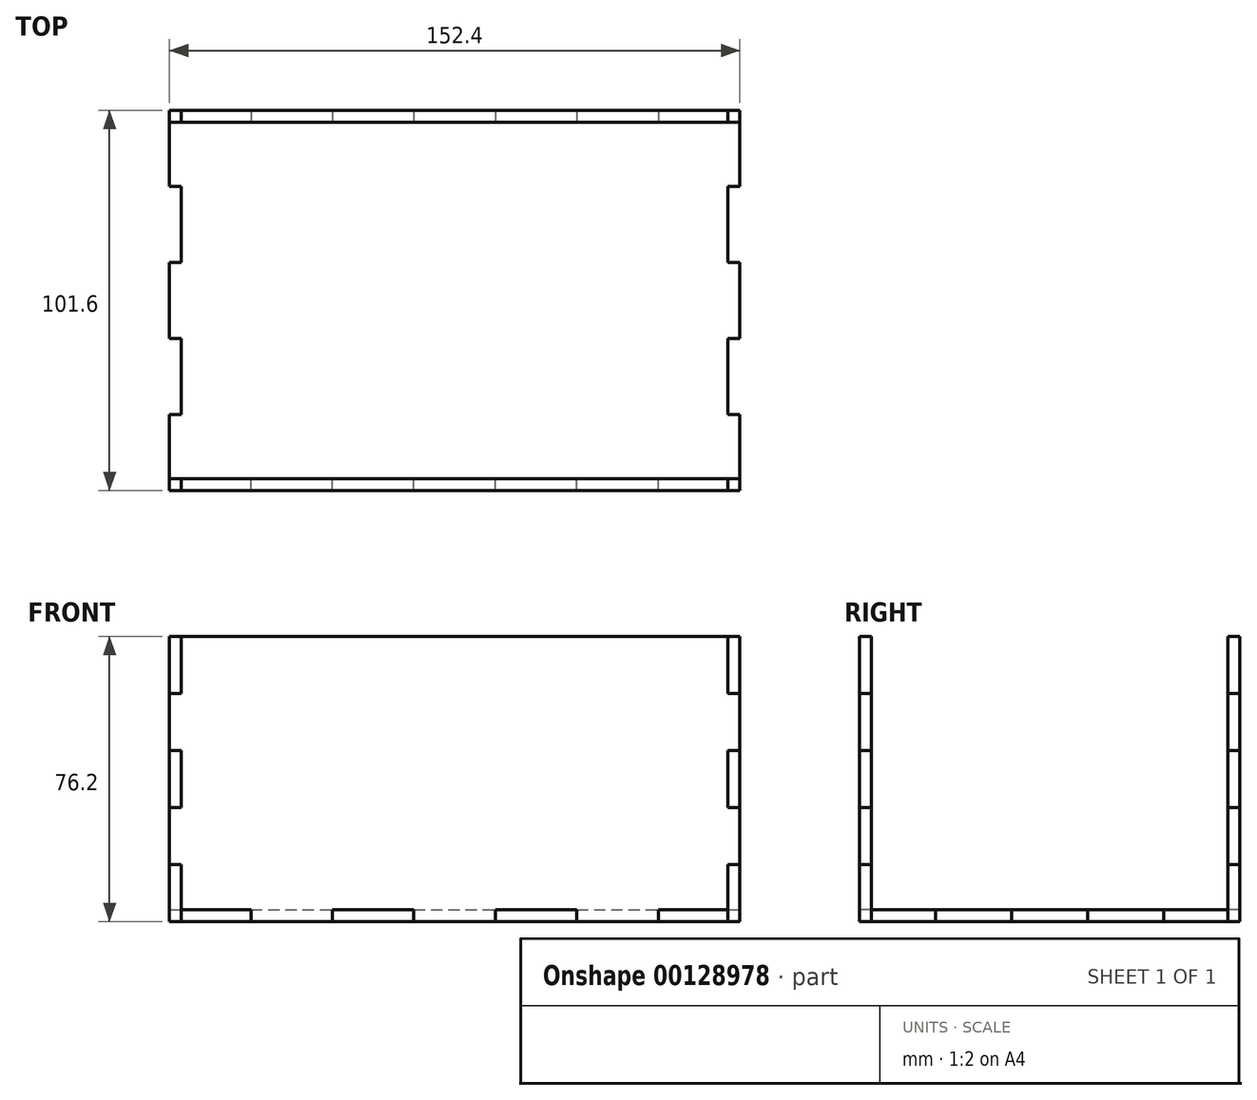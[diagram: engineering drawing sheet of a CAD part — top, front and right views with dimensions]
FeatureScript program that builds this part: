
annotation { "Feature Type Name" : "Feature", "Feature Type Description" : "" }
export const myFeature = defineFeature(function(context is Context, id is Id, definition is map)
    precondition{}
    {
        {
            var Q0;
            Q0=qCreatedBy(makeId("Top.planeOp"),FACE);
            var sketch = newSketch(context, id + "F0", { "sketchPlane" : qUnion([Q0])});
            skLineSegment(sketch, "E0.bottom", {"start": v(76.2, 50.8) * mm, "end": v(-76.2, 50.8) * mm});
            skLineSegment(sketch, "E0.top", {"start": v(76.2, -50.8) * mm, "end": v(-76.2, -50.8) * mm});
            skLineSegment(sketch, "E0.left", {"start": v(76.2, 50.8) * mm, "end": v(76.2, -50.8) * mm});
            skLineSegment(sketch, "E0.right", {"start": v(-76.2, 50.8) * mm, "end": v(-76.2, -50.8) * mm});
            skPoint(sketch, "E0.middle", {"position": v(0, 0) * mm});
            skLineSegment(sketch, "E1", {"start": v(-76.2, 50.8) * mm, "end": v(-73.03, 50.8) * mm});
            skLineSegment(sketch, "E2.0.1.0", {"start": v(-76.2, 30.48) * mm, "end": v(-73.03, 30.48) * mm});
            skLineSegment(sketch, "E2.0.2.0", {"start": v(-76.2, 10.16) * mm, "end": v(-73.03, 10.16) * mm});
            skLineSegment(sketch, "E2.0.3.0", {"start": v(-76.2, -10.16) * mm, "end": v(-73.02, -10.16) * mm});
            skLineSegment(sketch, "E2.0.4.0", {"start": v(-76.2, -30.48) * mm, "end": v(-73.02, -30.48) * mm});
            skLineSegment(sketch, "E2.0.5.0", {"start": v(-76.2, -50.8) * mm, "end": v(-73.02, -50.8) * mm});
            skLineSegment(sketch, "E2.direction1", {"start": v(-76.2, 50.8) * mm, "end": v(-50.8, 50.8) * mm, "construction": true});
            skLineSegment(sketch, "E2.direction2", {"start": v(-76.2, 50.8) * mm, "end": v(-76.2, 30.48) * mm, "construction": true});
            skLineSegment(sketch, "E3", {"start": v(-73.03, 50.8) * mm, "end": v(-73.03, -50.8) * mm});
            skLineSegment(sketch, "E4.MirrorCS", {"start": v(73.03, 50.8) * mm, "end": v(73.03, -50.8) * mm});
            skLineSegment(sketch, "E5.MirrorCS", {"start": v(76.2, 50.8) * mm, "end": v(76.2, 30.48) * mm, "construction": true});
            skLineSegment(sketch, "E6.MirrorCS", {"start": v(76.2, -50.8) * mm, "end": v(73.02, -50.8) * mm});
            skLineSegment(sketch, "E7.MirrorCS", {"start": v(76.2, -30.48) * mm, "end": v(73.02, -30.48) * mm});
            skLineSegment(sketch, "E8.MirrorCS", {"start": v(76.2, -10.16) * mm, "end": v(73.02, -10.16) * mm});
            skLineSegment(sketch, "E9.MirrorCS", {"start": v(76.2, 10.16) * mm, "end": v(73.03, 10.16) * mm});
            skLineSegment(sketch, "E10.MirrorCS", {"start": v(76.2, 30.48) * mm, "end": v(73.03, 30.48) * mm});
            skLineSegment(sketch, "E11.MirrorCS", {"start": v(76.2, 50.8) * mm, "end": v(73.03, 50.8) * mm});
            skLineSegment(sketch, "E12", {"start": v(-76.2, 50.8) * mm, "end": v(-76.2, 47.63) * mm});
            skLineSegment(sketch, "E13.1.0.0", {"start": v(-54.43, 50.8) * mm, "end": v(-54.43, 47.63) * mm});
            skLineSegment(sketch, "E13.2.0.0", {"start": v(-32.66, 50.8) * mm, "end": v(-32.66, 47.63) * mm});
            skLineSegment(sketch, "E13.3.0.0", {"start": v(-10.89, 50.8) * mm, "end": v(-10.89, 47.63) * mm});
            skLineSegment(sketch, "E13.4.0.0", {"start": v(10.89, 50.8) * mm, "end": v(10.89, 47.63) * mm});
            skLineSegment(sketch, "E13.5.0.0", {"start": v(32.66, 50.8) * mm, "end": v(32.66, 47.63) * mm});
            skLineSegment(sketch, "E13.6.0.0", {"start": v(54.43, 50.8) * mm, "end": v(54.43, 47.63) * mm});
            skLineSegment(sketch, "E13.7.0.0", {"start": v(76.2, 50.8) * mm, "end": v(76.2, 47.63) * mm});
            skLineSegment(sketch, "E13.direction1", {"start": v(-76.2, 47.62) * mm, "end": v(-54.43, 47.62) * mm, "construction": true});
            skLineSegment(sketch, "E14", {"start": v(-76.2, 47.62) * mm, "end": v(76.2, 47.63) * mm});
            skLineSegment(sketch, "E15.MirrorCS", {"start": v(-76.2, -50.8) * mm, "end": v(-76.2, -47.63) * mm});
            skLineSegment(sketch, "E16.MirrorCS", {"start": v(76.2, -50.8) * mm, "end": v(73.03, -50.8) * mm});
            skLineSegment(sketch, "E17.MirrorCS", {"start": v(-76.2, -50.8) * mm, "end": v(-73.03, -50.8) * mm});
            skLineSegment(sketch, "E18.MirrorCS", {"start": v(76.2, -50.8) * mm, "end": v(76.2, -47.63) * mm});
            skLineSegment(sketch, "E19.MirrorCS", {"start": v(-10.89, -50.8) * mm, "end": v(-10.89, -47.63) * mm});
            skLineSegment(sketch, "E20.MirrorCS", {"start": v(10.89, -50.8) * mm, "end": v(10.89, -47.63) * mm});
            skLineSegment(sketch, "E21.MirrorCS", {"start": v(54.43, -50.8) * mm, "end": v(54.43, -47.63) * mm});
            skLineSegment(sketch, "E22.MirrorCS", {"start": v(-32.66, -50.8) * mm, "end": v(-32.66, -47.63) * mm});
            skLineSegment(sketch, "E23.MirrorCS", {"start": v(-54.43, -50.8) * mm, "end": v(-54.43, -47.63) * mm});
            skLineSegment(sketch, "E24.MirrorCS", {"start": v(32.66, -50.8) * mm, "end": v(32.66, -47.63) * mm});
            skLineSegment(sketch, "E25.MirrorCS", {"start": v(-76.2, -47.62) * mm, "end": v(76.2, -47.63) * mm});
            skLineSegment(sketch, "E26.MirrorCS", {"start": v(-76.2, -47.62) * mm, "end": v(-54.43, -47.62) * mm, "construction": true});
            skLineSegment(sketch, "E27.MirrorCS", {"start": v(-76.2, -50.8) * mm, "end": v(-50.8, -50.8) * mm, "construction": true});
            skSolve(sketch);
        }
        {
            var Q0;
            {var subQ0=sQuery(id+"F0.wireOp",EDGE,"E1");Q0=makeQuery(id+"F0.imprint","IMPRINT",FACE,{"disambiguationData":[TD([[makeQuery(id+"F0.imprint","IMPRINT",EDGE,{"derivedFrom":subQ0}),-1.0]])]});}
            var Q1;
            {var subQ3=sQuery(id+"F0.wireOp",EDGE,"E13.1.0.0");Q1=makeQuery(id+"F0.imprint","IMPRINT",FACE,{"disambiguationData":[TD([[makeQuery(id+"F0.imprint","IMPRINT",EDGE,{"derivedFrom":subQ3}),-1.0]])]});}
            var Q2;
            {var subQ3=sQuery(id+"F0.wireOp",EDGE,"E2.0.1.0");Q2=makeQuery(id+"F0.imprint","IMPRINT",FACE,{"disambiguationData":[TD([[makeQuery(id+"F0.imprint","IMPRINT",EDGE,{"derivedFrom":subQ3}),1.0]])]});}
            var Q3;
            {var subQ4=sQuery(id+"F0.wireOp",EDGE,"E3");var subQ23=makeQuery(id+"F0.imprint","INTERSECT",VERTEX,{"derivedFrom":[sQuery(id+"F0.wireOp",EDGE,"E2.0.1.0"),subQ4]});Q3=makeQuery(id+"F0.imprint","IMPRINT",FACE,{"disambiguationData":[TD([[makeQuery(id+"F0.imprint","IMPRINT",EDGE,{"disambiguationData":[TD([[subQ23,1.0]])],"derivedFrom":subQ4}),1.0]])]});}
            var Q4;
            {var subQ0=sQuery(id+"F0.wireOp",EDGE,"E2.0.2.0");Q4=makeQuery(id+"F0.imprint","IMPRINT",FACE,{"disambiguationData":[TD([[makeQuery(id+"F0.imprint","IMPRINT",EDGE,{"derivedFrom":subQ0}),-1.0]])]});}
            var Q5;
            {var subQ3=sQuery(id+"F0.wireOp",EDGE,"E2.0.4.0");Q5=makeQuery(id+"F0.imprint","IMPRINT",FACE,{"disambiguationData":[TD([[makeQuery(id+"F0.imprint","IMPRINT",EDGE,{"derivedFrom":subQ3}),-1.0]])]});}
            var Q6;
            {var subQ5=sQuery(id+"F0.wireOp",EDGE,"E15.MirrorCS");Q6=makeQuery(id+"F0.imprint","IMPRINT",FACE,{"disambiguationData":[TD([[makeQuery(id+"F0.imprint","IMPRINT",EDGE,{"derivedFrom":subQ5}),-1.0]])]});}
            var Q7;
            {var subQ5=sQuery(id+"F0.wireOp",EDGE,"E23.MirrorCS");Q7=makeQuery(id+"F0.imprint","IMPRINT",FACE,{"disambiguationData":[TD([[makeQuery(id+"F0.imprint","IMPRINT",EDGE,{"derivedFrom":subQ5}),1.0]])]});}
            var Q8;
            {var subQ0=sQuery(id+"F0.wireOp",EDGE,"E19.MirrorCS");Q8=makeQuery(id+"F0.imprint","IMPRINT",FACE,{"disambiguationData":[TD([[makeQuery(id+"F0.imprint","IMPRINT",EDGE,{"derivedFrom":subQ0}),1.0]])]});}
            var Q9;
            {var subQ0=sQuery(id+"F0.wireOp",EDGE,"E20.MirrorCS");Q9=makeQuery(id+"F0.imprint","IMPRINT",FACE,{"disambiguationData":[TD([[makeQuery(id+"F0.imprint","IMPRINT",EDGE,{"derivedFrom":subQ0}),-1.0]])]});}
            var Q10;
            {var subQ5=sQuery(id+"F0.wireOp",EDGE,"E21.MirrorCS");Q10=makeQuery(id+"F0.imprint","IMPRINT",FACE,{"disambiguationData":[TD([[makeQuery(id+"F0.imprint","IMPRINT",EDGE,{"derivedFrom":subQ5}),-1.0]])]});}
            var Q11;
            {var subQ5=sQuery(id+"F0.wireOp",EDGE,"E18.MirrorCS");Q11=makeQuery(id+"F0.imprint","IMPRINT",FACE,{"disambiguationData":[TD([[makeQuery(id+"F0.imprint","IMPRINT",EDGE,{"derivedFrom":subQ5}),1.0]])]});}
            var Q12;
            {var subQ0=sQuery(id+"F0.wireOp",EDGE,"E7.MirrorCS");Q12=makeQuery(id+"F0.imprint","IMPRINT",FACE,{"disambiguationData":[TD([[makeQuery(id+"F0.imprint","IMPRINT",EDGE,{"derivedFrom":subQ0}),1.0]])]});}
            var Q13;
            {var subQ0=sQuery(id+"F0.wireOp",EDGE,"E8.MirrorCS");Q13=makeQuery(id+"F0.imprint","IMPRINT",FACE,{"disambiguationData":[TD([[makeQuery(id+"F0.imprint","IMPRINT",EDGE,{"derivedFrom":subQ0}),-1.0]])]});}
            var Q14;
            {var subQ0=sQuery(id+"F0.wireOp",EDGE,"E10.MirrorCS");Q14=makeQuery(id+"F0.imprint","IMPRINT",FACE,{"disambiguationData":[TD([[makeQuery(id+"F0.imprint","IMPRINT",EDGE,{"derivedFrom":subQ0}),-1.0]])]});}
            var Q15;
            {var subQ0=sQuery(id+"F0.wireOp",EDGE,"E11.MirrorCS");Q15=makeQuery(id+"F0.imprint","IMPRINT",FACE,{"disambiguationData":[TD([[makeQuery(id+"F0.imprint","IMPRINT",EDGE,{"derivedFrom":subQ0}),1.0]])]});}
            var Q16;
            {var subQ3=sQuery(id+"F0.wireOp",EDGE,"E13.6.0.0");Q16=makeQuery(id+"F0.imprint","IMPRINT",FACE,{"disambiguationData":[TD([[makeQuery(id+"F0.imprint","IMPRINT",EDGE,{"derivedFrom":subQ3}),1.0]])]});}
            var Q17;
            {var subQ0=sQuery(id+"F0.wireOp",EDGE,"E13.4.0.0");Q17=makeQuery(id+"F0.imprint","IMPRINT",FACE,{"disambiguationData":[TD([[makeQuery(id+"F0.imprint","IMPRINT",EDGE,{"derivedFrom":subQ0}),1.0]])]});}
            var Q18;
            {var subQ0=sQuery(id+"F0.wireOp",EDGE,"E13.2.0.0");Q18=makeQuery(id+"F0.imprint","IMPRINT",FACE,{"disambiguationData":[TD([[makeQuery(id+"F0.imprint","IMPRINT",EDGE,{"derivedFrom":subQ0}),1.0]])]});}
            extrude(context, id + "F1", {"entities" : qUnion([Q0, Q1, Q2, Q3, Q4, Q5, Q6, Q7, Q8, Q9, Q10, Q11, Q12, Q13, Q14, Q15, Q16, Q17, Q18]), "depth" : 3.17 * mm});
        }
        {
            var Q0;
            Q0=makeQuery(id+"F1.opExtrude","SWEPT_FACE",FACE,{"disambiguationData":[OSD([sQuery(id+"F0.wireOp",EDGE,"E0.left"),sQuery(id+"F0.wireOp",EDGE,"E18.MirrorCS")])]});
            var sketch = newSketch(context, id + "F2", { "sketchPlane" : qUnion([Q0])});
            skLineSegment(sketch, "E28.bottom", {"start": v(-50.8, 0) * mm, "end": v(50.8, 0) * mm});
            skLineSegment(sketch, "E28.top", {"start": v(-50.8, 76.2) * mm, "end": v(50.8, 76.2) * mm});
            skLineSegment(sketch, "E28.left", {"start": v(-50.8, 0) * mm, "end": v(-50.8, 76.2) * mm});
            skLineSegment(sketch, "E28.right", {"start": v(50.8, 0) * mm, "end": v(50.8, 76.2) * mm});
            skLineSegment(sketch, "E29", {"start": v(-50.8, 76.2) * mm, "end": v(-47.62, 76.2) * mm});
            skLineSegment(sketch, "E30.0.1.0", {"start": v(-50.8, 60.96) * mm, "end": v(-47.62, 60.96) * mm});
            skLineSegment(sketch, "E30.0.2.0", {"start": v(-50.8, 45.72) * mm, "end": v(-47.62, 45.72) * mm});
            skLineSegment(sketch, "E30.0.3.0", {"start": v(-50.8, 30.48) * mm, "end": v(-47.62, 30.48) * mm});
            skLineSegment(sketch, "E30.0.4.0", {"start": v(-50.8, 15.24) * mm, "end": v(-47.62, 15.24) * mm});
            skLineSegment(sketch, "E30.0.5.0", {"start": v(-50.8, 0) * mm, "end": v(-47.62, 0) * mm});
            skLineSegment(sketch, "E30.direction1", {"start": v(-50.8, 76.2) * mm, "end": v(-25.4, 76.2) * mm, "construction": true});
            skLineSegment(sketch, "E30.direction2", {"start": v(-50.8, 76.2) * mm, "end": v(-50.8, 60.96) * mm, "construction": true});
            skLineSegment(sketch, "E31", {"start": v(-47.62, 76.2) * mm, "end": v(-47.62, 0) * mm});
            skLineSegment(sketch, "E32.MirrorCS", {"start": v(50.8, 76.2) * mm, "end": v(47.63, 76.2) * mm});
            skLineSegment(sketch, "E33.MirrorCS", {"start": v(50.8, 30.48) * mm, "end": v(47.63, 30.48) * mm});
            skLineSegment(sketch, "E34.MirrorCS", {"start": v(50.8, 60.96) * mm, "end": v(47.63, 60.96) * mm});
            skLineSegment(sketch, "E35.MirrorCS", {"start": v(50.8, 45.72) * mm, "end": v(47.63, 45.72) * mm});
            skLineSegment(sketch, "E36.MirrorCS", {"start": v(50.8, 15.24) * mm, "end": v(47.63, 15.24) * mm});
            skLineSegment(sketch, "E37.MirrorCS", {"start": v(50.8, 0) * mm, "end": v(47.63, 0) * mm});
            skLineSegment(sketch, "E38.MirrorCS", {"start": v(50.8, 76.2) * mm, "end": v(50.8, 60.96) * mm, "construction": true});
            skLineSegment(sketch, "E39.MirrorCS", {"start": v(47.63, 76.2) * mm, "end": v(47.63, 0) * mm});
            skSolve(sketch);
        }
        {
            var Q0;
            {var subQ0=sQuery(id+"F2.wireOp",EDGE,"E29");Q0=makeQuery(id+"F2.imprint","IMPRINT",FACE,{"disambiguationData":[TD([[makeQuery(id+"F2.imprint","IMPRINT",EDGE,{"derivedFrom":subQ0}),-1.0]])]});}
            var Q1;
            {var subQ3=sQuery(id+"F2.wireOp",EDGE,"E28.top");Q1=makeQuery(id+"F2.imprint","IMPRINT",FACE,{"disambiguationData":[TD([[makeQuery(id+"F2.imprint","IMPRINT",EDGE,{"derivedFrom":subQ3}),-1.0]])]});}
            var Q2;
            {var subQ0=sQuery(id+"F2.wireOp",EDGE,"E30.0.2.0");Q2=makeQuery(id+"F2.imprint","IMPRINT",FACE,{"disambiguationData":[TD([[makeQuery(id+"F2.imprint","IMPRINT",EDGE,{"derivedFrom":subQ0}),-1.0]])]});}
            var Q3;
            {var subQ3=sQuery(id+"F2.wireOp",EDGE,"E30.0.4.0");Q3=makeQuery(id+"F2.imprint","IMPRINT",FACE,{"disambiguationData":[TD([[makeQuery(id+"F2.imprint","IMPRINT",EDGE,{"derivedFrom":subQ3}),-1.0]])]});}
            var Q4;
            {var subQ0=sQuery(id+"F2.wireOp",EDGE,"E30.0.5.0");Q4=makeQuery(id+"F2.imprint","IMPRINT",FACE,{"disambiguationData":[TD([[makeQuery(id+"F2.imprint","IMPRINT",EDGE,{"derivedFrom":subQ0}),1.0]])]});}
            var Q5;
            {var subQ1=sQuery(id+"F0.wireOp",EDGE,"E0.left");var subQ2=makeQuery(id+"F1.opExtrude","SWEPT_EDGE",EDGE,{"disambiguationData":[OSD([sQuery(id+"F0.wireOp",EDGE,"E7.MirrorCS"),subQ1])]});Q5=makeQuery(id+"F2.imprint","IMPRINT",FACE,{"disambiguationData":[TD([[makeQuery(id+"F2.imprint","IMPRINT",EDGE,{"derivedFrom":subQ2}),-1.0]])]});}
            var Q6;
            {var subQ2=sQuery(id+"F2.wireOp",EDGE,"E36.MirrorCS");Q6=makeQuery(id+"F2.imprint","IMPRINT",FACE,{"disambiguationData":[TD([[makeQuery(id+"F2.imprint","IMPRINT",EDGE,{"derivedFrom":subQ2}),1.0]])]});}
            var Q7;
            {var subQ0=sQuery(id+"F2.wireOp",EDGE,"E33.MirrorCS");Q7=makeQuery(id+"F2.imprint","IMPRINT",FACE,{"disambiguationData":[TD([[makeQuery(id+"F2.imprint","IMPRINT",EDGE,{"derivedFrom":subQ0}),-1.0]])]});}
            var Q8;
            {var subQ0=sQuery(id+"F2.wireOp",EDGE,"E32.MirrorCS");Q8=makeQuery(id+"F2.imprint","IMPRINT",FACE,{"disambiguationData":[TD([[makeQuery(id+"F2.imprint","IMPRINT",EDGE,{"derivedFrom":subQ0}),1.0]])]});}
            extrude(context, id + "F3", {"entities" : qUnion([Q0, Q1, Q2, Q3, Q4, Q5, Q6, Q7, Q8]), "oppositeDirection" : true, "depth" : 3.17 * mm});
        }
        {
            var Q0;
            Q0=makeQuery(id+"F3.opExtrude","SWEPT_BODY",BODY,{"disambiguationData":[OSD([sQuery(id+"F2.wireOp",EDGE,"E28.bottom"),sQuery(id+"F2.wireOp",EDGE,"E28.top"),sQuery(id+"F2.wireOp",EDGE,"E28.left"),sQuery(id+"F2.wireOp",EDGE,"E29"),sQuery(id+"F2.wireOp",EDGE,"E30.0.1.0"),sQuery(id+"F2.wireOp",EDGE,"E30.0.2.0"),sQuery(id+"F2.wireOp",EDGE,"E30.0.3.0"),sQuery(id+"F2.wireOp",EDGE,"E30.0.4.0"),sQuery(id+"F2.wireOp",EDGE,"E30.0.5.0"),sQuery(id+"F2.wireOp",EDGE,"E31"),sQuery(id+"F2.wireOp",EDGE,"E28.right"),sQuery(id+"F2.wireOp",EDGE,"E32.MirrorCS"),sQuery(id+"F2.wireOp",EDGE,"E33.MirrorCS"),sQuery(id+"F2.wireOp",EDGE,"E34.MirrorCS"),sQuery(id+"F2.wireOp",EDGE,"E35.MirrorCS"),sQuery(id+"F2.wireOp",EDGE,"E36.MirrorCS"),sQuery(id+"F2.wireOp",EDGE,"E37.MirrorCS"),sQuery(id+"F2.wireOp",EDGE,"E39.MirrorCS")])]});
            var Q1;
            Q1=qCreatedBy(makeId("Right.planeOp"),FACE);
            mirror(context, id + "F4", {"entities" : qUnion([Q0]), "mirrorPlane" : qUnion([Q1])});
        }
        {
            var Q0;
            Q0=makeQuery(id+"F1.opExtrude","SWEPT_BODY",BODY,{"disambiguationData":[OSD([sQuery(id+"F0.wireOp",EDGE,"E0.bottom"),sQuery(id+"F0.wireOp",EDGE,"E0.right"),sQuery(id+"F0.wireOp",EDGE,"E1"),sQuery(id+"F0.wireOp",EDGE,"E2.0.1.0"),sQuery(id+"F0.wireOp",EDGE,"E2.0.2.0"),sQuery(id+"F0.wireOp",EDGE,"E2.0.3.0"),sQuery(id+"F0.wireOp",EDGE,"E2.0.4.0"),sQuery(id+"F0.wireOp",EDGE,"E3"),sQuery(id+"F0.wireOp",EDGE,"E4.MirrorCS"),sQuery(id+"F0.wireOp",EDGE,"E7.MirrorCS"),sQuery(id+"F0.wireOp",EDGE,"E0.left"),sQuery(id+"F0.wireOp",EDGE,"E8.MirrorCS"),sQuery(id+"F0.wireOp",EDGE,"E9.MirrorCS"),sQuery(id+"F0.wireOp",EDGE,"E10.MirrorCS"),sQuery(id+"F0.wireOp",EDGE,"E11.MirrorCS"),sQuery(id+"F0.wireOp",EDGE,"E12"),sQuery(id+"F0.wireOp",EDGE,"E13.1.0.0"),sQuery(id+"F0.wireOp",EDGE,"E13.2.0.0"),sQuery(id+"F0.wireOp",EDGE,"E13.3.0.0"),sQuery(id+"F0.wireOp",EDGE,"E13.4.0.0"),sQuery(id+"F0.wireOp",EDGE,"E13.5.0.0"),sQuery(id+"F0.wireOp",EDGE,"E13.6.0.0"),sQuery(id+"F0.wireOp",EDGE,"E13.7.0.0"),sQuery(id+"F0.wireOp",EDGE,"E14"),sQuery(id+"F0.wireOp",EDGE,"E15.MirrorCS"),sQuery(id+"F0.wireOp",EDGE,"E18.MirrorCS"),sQuery(id+"F0.wireOp",EDGE,"E19.MirrorCS"),sQuery(id+"F0.wireOp",EDGE,"E20.MirrorCS"),sQuery(id+"F0.wireOp",EDGE,"E21.MirrorCS"),sQuery(id+"F0.wireOp",EDGE,"E22.MirrorCS"),sQuery(id+"F0.wireOp",EDGE,"E23.MirrorCS"),sQuery(id+"F0.wireOp",EDGE,"E24.MirrorCS"),sQuery(id+"F0.wireOp",EDGE,"E25.MirrorCS"),sQuery(id+"F0.wireOp",EDGE,"E0.top")])]});
            var Q1;
            Q1=makeQuery(id+"F3.opExtrude","SWEPT_BODY",BODY,{"disambiguationData":[OSD([sQuery(id+"F2.wireOp",EDGE,"E28.bottom"),sQuery(id+"F2.wireOp",EDGE,"E28.top"),sQuery(id+"F2.wireOp",EDGE,"E28.left"),sQuery(id+"F2.wireOp",EDGE,"E29"),sQuery(id+"F2.wireOp",EDGE,"E30.0.1.0"),sQuery(id+"F2.wireOp",EDGE,"E30.0.2.0"),sQuery(id+"F2.wireOp",EDGE,"E30.0.3.0"),sQuery(id+"F2.wireOp",EDGE,"E30.0.4.0"),sQuery(id+"F2.wireOp",EDGE,"E30.0.5.0"),sQuery(id+"F2.wireOp",EDGE,"E31"),sQuery(id+"F2.wireOp",EDGE,"E28.right"),sQuery(id+"F2.wireOp",EDGE,"E32.MirrorCS"),sQuery(id+"F2.wireOp",EDGE,"E33.MirrorCS"),sQuery(id+"F2.wireOp",EDGE,"E34.MirrorCS"),sQuery(id+"F2.wireOp",EDGE,"E35.MirrorCS"),sQuery(id+"F2.wireOp",EDGE,"E36.MirrorCS"),sQuery(id+"F2.wireOp",EDGE,"E37.MirrorCS"),sQuery(id+"F2.wireOp",EDGE,"E39.MirrorCS")])]});
            var Q2;
            Q2=makeQuery(id+"F4.opPattern","COPY",BODY,{"derivedFrom":makeQuery(id+"F3.opExtrude","SWEPT_BODY",BODY,{"disambiguationData":[OSD([sQuery(id+"F2.wireOp",EDGE,"E28.bottom"),sQuery(id+"F2.wireOp",EDGE,"E28.top"),sQuery(id+"F2.wireOp",EDGE,"E28.left"),sQuery(id+"F2.wireOp",EDGE,"E29"),sQuery(id+"F2.wireOp",EDGE,"E30.0.1.0"),sQuery(id+"F2.wireOp",EDGE,"E30.0.2.0"),sQuery(id+"F2.wireOp",EDGE,"E30.0.3.0"),sQuery(id+"F2.wireOp",EDGE,"E30.0.4.0"),sQuery(id+"F2.wireOp",EDGE,"E30.0.5.0"),sQuery(id+"F2.wireOp",EDGE,"E31"),sQuery(id+"F2.wireOp",EDGE,"E28.right"),sQuery(id+"F2.wireOp",EDGE,"E32.MirrorCS"),sQuery(id+"F2.wireOp",EDGE,"E33.MirrorCS"),sQuery(id+"F2.wireOp",EDGE,"E34.MirrorCS"),sQuery(id+"F2.wireOp",EDGE,"E35.MirrorCS"),sQuery(id+"F2.wireOp",EDGE,"E36.MirrorCS"),sQuery(id+"F2.wireOp",EDGE,"E37.MirrorCS"),sQuery(id+"F2.wireOp",EDGE,"E39.MirrorCS")])]}),"instanceName":"1"});
            booleanBodies(context, id + "F5", {"operationType" : BooleanOperationType.SUBTRACTION, "tools" : qUnion([Q0]), "targets" : qUnion([Q1, Q2]), "keepTools" : true});
        }
        {
            var Q0;
            Q0=makeQuery(id+"F1.opExtrude","SWEPT_FACE",FACE,{"disambiguationData":[OSD([sQuery(id+"F0.wireOp",EDGE,"E0.bottom"),sQuery(id+"F0.wireOp",EDGE,"E11.MirrorCS")])]});
            var sketch = newSketch(context, id + "F6", { "sketchPlane" : qUnion([Q0])});
            skLineSegment(sketch, "E40.bottom", {"start": v(-76.2, 0) * mm, "end": v(76.2, 0) * mm});
            skLineSegment(sketch, "E40.top", {"start": v(-76.2, 76.2) * mm, "end": v(76.2, 76.2) * mm});
            skLineSegment(sketch, "E40.left", {"start": v(-76.2, 0) * mm, "end": v(-76.2, 76.2) * mm});
            skLineSegment(sketch, "E40.right", {"start": v(76.2, 0) * mm, "end": v(76.2, 76.2) * mm});
            skSolve(sketch);
        }
        {
            var Q0;
            {var subQ4=sQuery(id+"F6.wireOp",EDGE,"E40.top");Q0=makeQuery(id+"F6.imprint","IMPRINT",FACE,{"disambiguationData":[TD([[makeQuery(id+"F6.imprint","IMPRINT",EDGE,{"derivedFrom":subQ4}),-1.0]])]});}
            extrude(context, id + "F7", {"entities" : qUnion([Q0]), "oppositeDirection" : true, "depth" : 3.17 * mm});
        }
        {
            var Q0;
            Q0=makeQuery(id+"F7.opExtrude","SWEPT_BODY",BODY,{"disambiguationData":[OSD([sQuery(id+"F0.wireOp",EDGE,"E0.bottom"),sQuery(id+"F0.wireOp",EDGE,"E11.MirrorCS"),sQuery(id+"F0.wireOp",EDGE,"E13.6.0.0"),sQuery(id+"F6.wireOp",EDGE,"E40.bottom"),sQuery(id+"F6.wireOp",EDGE,"E40.top"),sQuery(id+"F6.wireOp",EDGE,"E40.left"),sQuery(id+"F6.wireOp",EDGE,"E40.right")])]});
            var Q1;
            Q1=qCreatedBy(makeId("Front.planeOp"),FACE);
            mirror(context, id + "F8", {"entities" : qUnion([Q0]), "mirrorPlane" : qUnion([Q1])});
        }
        {
            var Q0;
            Q0=makeQuery(id+"F3.opExtrude","SWEPT_BODY",BODY,{"disambiguationData":[OSD([sQuery(id+"F2.wireOp",EDGE,"E28.bottom"),sQuery(id+"F2.wireOp",EDGE,"E28.top"),sQuery(id+"F2.wireOp",EDGE,"E28.left"),sQuery(id+"F2.wireOp",EDGE,"E29"),sQuery(id+"F2.wireOp",EDGE,"E30.0.1.0"),sQuery(id+"F2.wireOp",EDGE,"E30.0.2.0"),sQuery(id+"F2.wireOp",EDGE,"E30.0.3.0"),sQuery(id+"F2.wireOp",EDGE,"E30.0.4.0"),sQuery(id+"F2.wireOp",EDGE,"E30.0.5.0"),sQuery(id+"F2.wireOp",EDGE,"E31"),sQuery(id+"F2.wireOp",EDGE,"E28.right"),sQuery(id+"F2.wireOp",EDGE,"E32.MirrorCS"),sQuery(id+"F2.wireOp",EDGE,"E33.MirrorCS"),sQuery(id+"F2.wireOp",EDGE,"E34.MirrorCS"),sQuery(id+"F2.wireOp",EDGE,"E35.MirrorCS"),sQuery(id+"F2.wireOp",EDGE,"E36.MirrorCS"),sQuery(id+"F2.wireOp",EDGE,"E37.MirrorCS"),sQuery(id+"F2.wireOp",EDGE,"E39.MirrorCS")])]});
            var Q1;
            Q1=makeQuery(id+"F4.opPattern","COPY",BODY,{"derivedFrom":makeQuery(id+"F3.opExtrude","SWEPT_BODY",BODY,{"disambiguationData":[OSD([sQuery(id+"F2.wireOp",EDGE,"E28.bottom"),sQuery(id+"F2.wireOp",EDGE,"E28.top"),sQuery(id+"F2.wireOp",EDGE,"E28.left"),sQuery(id+"F2.wireOp",EDGE,"E29"),sQuery(id+"F2.wireOp",EDGE,"E30.0.1.0"),sQuery(id+"F2.wireOp",EDGE,"E30.0.2.0"),sQuery(id+"F2.wireOp",EDGE,"E30.0.3.0"),sQuery(id+"F2.wireOp",EDGE,"E30.0.4.0"),sQuery(id+"F2.wireOp",EDGE,"E30.0.5.0"),sQuery(id+"F2.wireOp",EDGE,"E31"),sQuery(id+"F2.wireOp",EDGE,"E28.right"),sQuery(id+"F2.wireOp",EDGE,"E32.MirrorCS"),sQuery(id+"F2.wireOp",EDGE,"E33.MirrorCS"),sQuery(id+"F2.wireOp",EDGE,"E34.MirrorCS"),sQuery(id+"F2.wireOp",EDGE,"E35.MirrorCS"),sQuery(id+"F2.wireOp",EDGE,"E36.MirrorCS"),sQuery(id+"F2.wireOp",EDGE,"E37.MirrorCS"),sQuery(id+"F2.wireOp",EDGE,"E39.MirrorCS")])]}),"instanceName":"1"});
            var Q2;
            Q2=makeQuery(id+"F1.opExtrude","SWEPT_BODY",BODY,{"disambiguationData":[OSD([sQuery(id+"F0.wireOp",EDGE,"E0.bottom"),sQuery(id+"F0.wireOp",EDGE,"E0.right"),sQuery(id+"F0.wireOp",EDGE,"E1"),sQuery(id+"F0.wireOp",EDGE,"E2.0.1.0"),sQuery(id+"F0.wireOp",EDGE,"E2.0.2.0"),sQuery(id+"F0.wireOp",EDGE,"E2.0.3.0"),sQuery(id+"F0.wireOp",EDGE,"E2.0.4.0"),sQuery(id+"F0.wireOp",EDGE,"E3"),sQuery(id+"F0.wireOp",EDGE,"E4.MirrorCS"),sQuery(id+"F0.wireOp",EDGE,"E7.MirrorCS"),sQuery(id+"F0.wireOp",EDGE,"E0.left"),sQuery(id+"F0.wireOp",EDGE,"E8.MirrorCS"),sQuery(id+"F0.wireOp",EDGE,"E9.MirrorCS"),sQuery(id+"F0.wireOp",EDGE,"E10.MirrorCS"),sQuery(id+"F0.wireOp",EDGE,"E11.MirrorCS"),sQuery(id+"F0.wireOp",EDGE,"E12"),sQuery(id+"F0.wireOp",EDGE,"E13.1.0.0"),sQuery(id+"F0.wireOp",EDGE,"E13.2.0.0"),sQuery(id+"F0.wireOp",EDGE,"E13.3.0.0"),sQuery(id+"F0.wireOp",EDGE,"E13.4.0.0"),sQuery(id+"F0.wireOp",EDGE,"E13.5.0.0"),sQuery(id+"F0.wireOp",EDGE,"E13.6.0.0"),sQuery(id+"F0.wireOp",EDGE,"E13.7.0.0"),sQuery(id+"F0.wireOp",EDGE,"E14"),sQuery(id+"F0.wireOp",EDGE,"E15.MirrorCS"),sQuery(id+"F0.wireOp",EDGE,"E18.MirrorCS"),sQuery(id+"F0.wireOp",EDGE,"E19.MirrorCS"),sQuery(id+"F0.wireOp",EDGE,"E20.MirrorCS"),sQuery(id+"F0.wireOp",EDGE,"E21.MirrorCS"),sQuery(id+"F0.wireOp",EDGE,"E22.MirrorCS"),sQuery(id+"F0.wireOp",EDGE,"E23.MirrorCS"),sQuery(id+"F0.wireOp",EDGE,"E24.MirrorCS"),sQuery(id+"F0.wireOp",EDGE,"E25.MirrorCS"),sQuery(id+"F0.wireOp",EDGE,"E0.top")])]});
            var Q3;
            Q3=makeQuery(id+"F8.opPattern","COPY",BODY,{"derivedFrom":makeQuery(id+"F7.opExtrude","SWEPT_BODY",BODY,{"disambiguationData":[OSD([sQuery(id+"F0.wireOp",EDGE,"E0.bottom"),sQuery(id+"F0.wireOp",EDGE,"E11.MirrorCS"),sQuery(id+"F0.wireOp",EDGE,"E13.6.0.0"),sQuery(id+"F6.wireOp",EDGE,"E40.bottom"),sQuery(id+"F6.wireOp",EDGE,"E40.top"),sQuery(id+"F6.wireOp",EDGE,"E40.left"),sQuery(id+"F6.wireOp",EDGE,"E40.right")])]}),"instanceName":"1"});
            var Q4;
            Q4=makeQuery(id+"F7.opExtrude","SWEPT_BODY",BODY,{"disambiguationData":[OSD([sQuery(id+"F0.wireOp",EDGE,"E0.bottom"),sQuery(id+"F0.wireOp",EDGE,"E11.MirrorCS"),sQuery(id+"F0.wireOp",EDGE,"E13.6.0.0"),sQuery(id+"F6.wireOp",EDGE,"E40.bottom"),sQuery(id+"F6.wireOp",EDGE,"E40.top"),sQuery(id+"F6.wireOp",EDGE,"E40.left"),sQuery(id+"F6.wireOp",EDGE,"E40.right")])]});
            booleanBodies(context, id + "F9", {"operationType" : BooleanOperationType.SUBTRACTION, "tools" : qUnion([Q0, Q1, Q2]), "targets" : qUnion([Q3, Q4]), "keepTools" : true});
        }
    });
